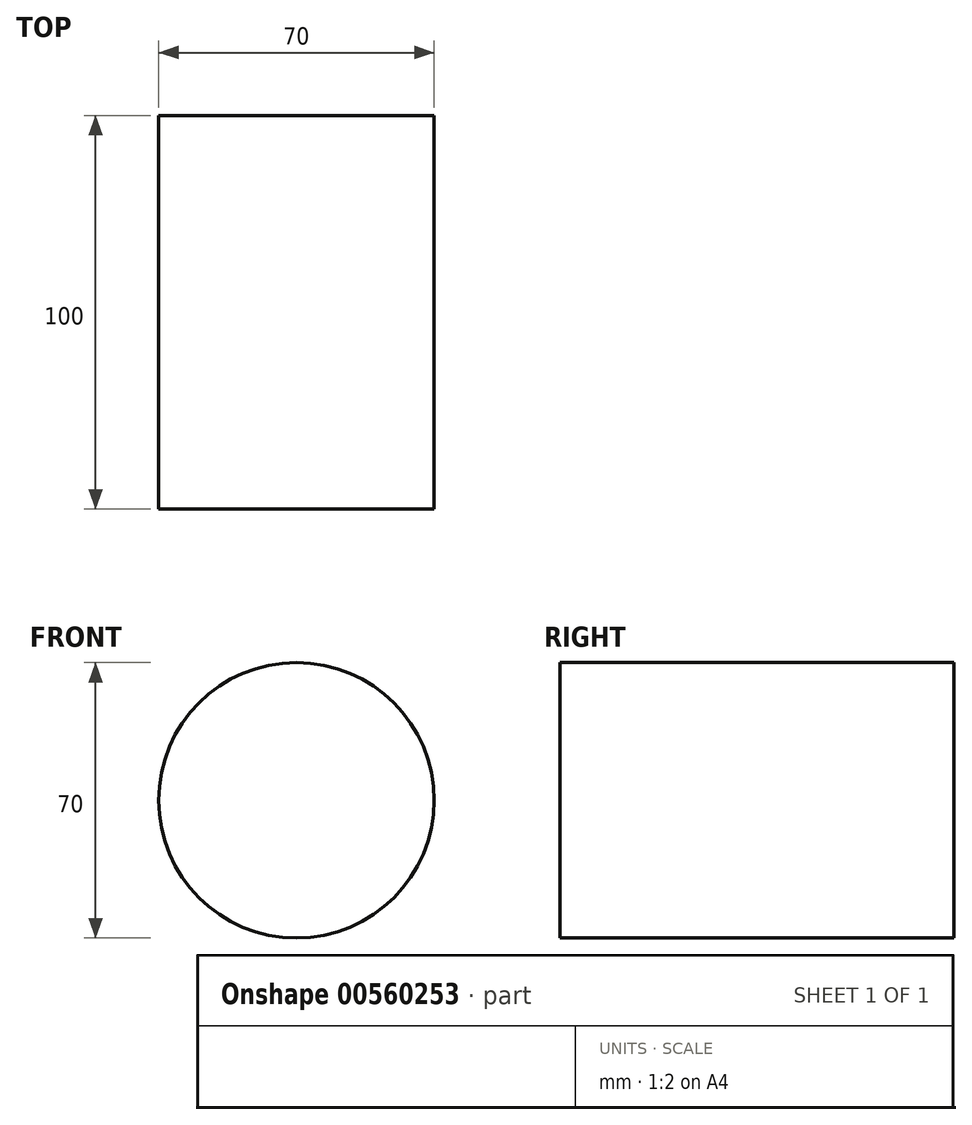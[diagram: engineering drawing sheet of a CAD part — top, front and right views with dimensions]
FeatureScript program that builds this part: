
annotation { "Feature Type Name" : "Feature", "Feature Type Description" : "" }
export const myFeature = defineFeature(function(context is Context, id is Id, definition is map)
    precondition{}
    {
        {
            var Q0;
            Q0=qCreatedBy(makeId("Front.planeOp"),FACE);
            var sketch = newSketch(context, id + "F0", { "sketchPlane" : qUnion([Q0])});
            skCircle(sketch, "E0", {"center": v(0, 0) * mm, "radius": 35 * mm});
            skSolve(sketch);
        }
        {
            var Q0;
            Q0=makeQuery(id+"F0.imprint","IMPRINT",FACE,{"disambiguationData":[TD([[makeQuery(id+"F0.imprint","IMPRINT",EDGE,{"derivedFrom":sQuery(id+"F0.wireOp",EDGE,"E0")}),1.0]])]});
            extrude(context, id + "F1", {"entities" : qUnion([Q0]), "depth" : 100 * mm, "offsetDistance" : 25 * mm});
        }
    });
